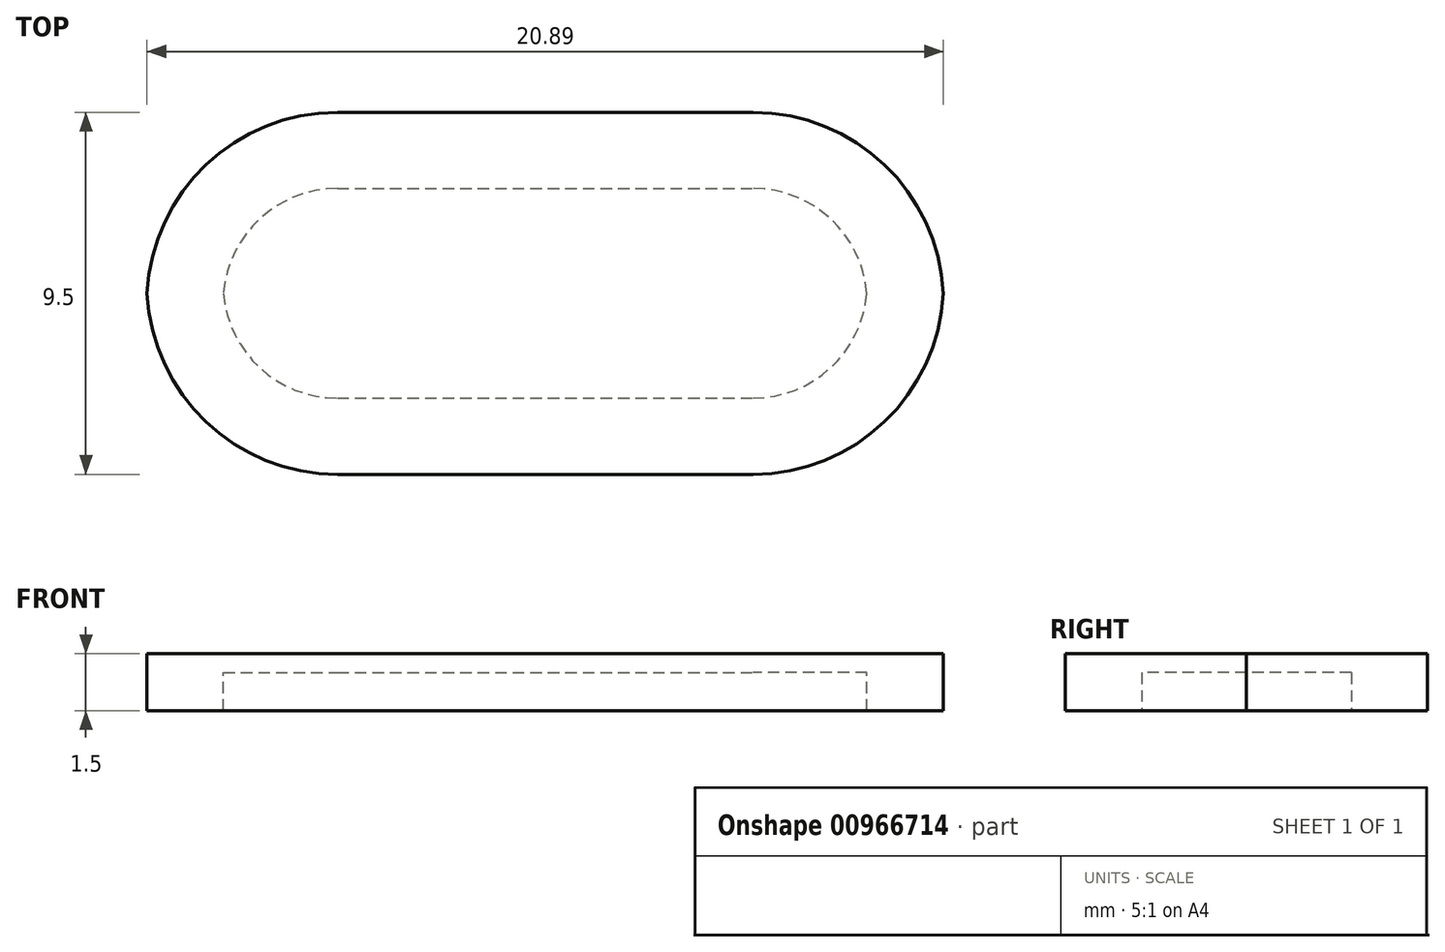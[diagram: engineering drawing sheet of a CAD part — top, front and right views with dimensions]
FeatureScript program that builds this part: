
annotation { "Feature Type Name" : "Feature", "Feature Type Description" : "" }
export const myFeature = defineFeature(function(context is Context, id is Id, definition is map)
    precondition{}
    {
        {
            var Q0;
            Q0=qCreatedBy(makeId("Top.planeOp"),FACE);
            var sketch = newSketch(context, id + "F0", { "sketchPlane" : qUnion([Q0])});
            skLineSegment(sketch, "E0.bottom", {"start": v(-10.3, 4.13) * mm, "end": v(10.6, 4.13) * mm});
            skLineSegment(sketch, "E0.top", {"start": v(-10.3, -5.37) * mm, "end": v(10.6, -5.37) * mm});
            skLineSegment(sketch, "E0.left", {"start": v(-10.3, 4.13) * mm, "end": v(-10.3, -5.37) * mm});
            skLineSegment(sketch, "E0.right", {"start": v(10.6, 4.13) * mm, "end": v(10.6, -5.37) * mm});
            skSolve(sketch);
        }
        {
            var Q0;
            Q0 = qSketchRegion(id + "F0", true);
            extrude(context, id + "F1", {"entities" : qUnion([Q0]), "depth" : 1.5 * mm, "offsetDistance" : 25 * mm});
        }
        {
            var Q0;
            Q0=qCreatedBy(makeId("Top.planeOp"),FACE);
            var sketch = newSketch(context, id + "F2", { "sketchPlane" : qUnion([Q0])});
            skLineSegment(sketch, "E1.bottom", {"start": v(-8.3, 2.13) * mm, "end": v(8.6, 2.13) * mm});
            skLineSegment(sketch, "E1.top", {"start": v(-8.3, -3.37) * mm, "end": v(8.6, -3.37) * mm});
            skLineSegment(sketch, "E1.left", {"start": v(-8.3, 2.13) * mm, "end": v(-8.3, -3.37) * mm});
            skLineSegment(sketch, "E1.right", {"start": v(8.6, 2.13) * mm, "end": v(8.6, -3.37) * mm});
            skSolve(sketch);
        }
        {
            var Q0;
            Q0 = qSketchRegion(id + "F2", true);
            extrude(context, id + "F3", {"entities" : qUnion([Q0]), "operationType" : NewBodyOperationType.REMOVE, "depth" : 1 * mm, "offsetDistance" : 25 * mm});
        }
        {
            var Q0;
            Q0=makeQuery(id+"F3.boolean.opBoolean","COPY",EDGE,{"derivedFrom":makeQuery(id+"F3.opExtrude","SWEPT_EDGE",EDGE,{"disambiguationData":[OSD([sQuery(id+"F2.wireOp",EDGE,"E1.top"),sQuery(id+"F2.wireOp",EDGE,"E1.right")])]})});
            var Q1;
            Q1=makeQuery(id+"F3.boolean.opBoolean","COPY",EDGE,{"derivedFrom":makeQuery(id+"F3.opExtrude","SWEPT_EDGE",EDGE,{"disambiguationData":[OSD([sQuery(id+"F2.wireOp",EDGE,"E1.bottom"),sQuery(id+"F2.wireOp",EDGE,"E1.left")])]})});
            var Q2;
            Q2=makeQuery(id+"F3.boolean.opBoolean","COPY",EDGE,{"derivedFrom":makeQuery(id+"F3.opExtrude","SWEPT_EDGE",EDGE,{"disambiguationData":[OSD([sQuery(id+"F2.wireOp",EDGE,"E1.bottom"),sQuery(id+"F2.wireOp",EDGE,"E1.right")])]})});
            var Q3;
            Q3=makeQuery(id+"F3.boolean.opBoolean","COPY",EDGE,{"derivedFrom":makeQuery(id+"F3.opExtrude","SWEPT_EDGE",EDGE,{"disambiguationData":[OSD([sQuery(id+"F2.wireOp",EDGE,"E1.top"),sQuery(id+"F2.wireOp",EDGE,"E1.left")])]})});
            fillet(context, id + "F4", {"entities" : qUnion([Q0, Q1, Q2, Q3]), "radius" : 3 * mm, "tangentPropagation" : true, "allowEdgeOverflow" : false});
        }
        {
            var Q0;
            Q0=makeQuery(id+"F1.opExtrude","SWEPT_EDGE",EDGE,{"disambiguationData":[OSD([sQuery(id+"F0.wireOp",EDGE,"E0.bottom"),sQuery(id+"F0.wireOp",EDGE,"E0.left")])]});
            var Q1;
            Q1=makeQuery(id+"F1.opExtrude","SWEPT_EDGE",EDGE,{"disambiguationData":[OSD([sQuery(id+"F0.wireOp",EDGE,"E0.top"),sQuery(id+"F0.wireOp",EDGE,"E0.left")])]});
            var Q2;
            Q2=makeQuery(id+"F1.opExtrude","SWEPT_EDGE",EDGE,{"disambiguationData":[OSD([sQuery(id+"F0.wireOp",EDGE,"E0.bottom"),sQuery(id+"F0.wireOp",EDGE,"E0.right")])]});
            var Q3;
            Q3=makeQuery(id+"F1.opExtrude","SWEPT_EDGE",EDGE,{"disambiguationData":[OSD([sQuery(id+"F0.wireOp",EDGE,"E0.top"),sQuery(id+"F0.wireOp",EDGE,"E0.right")])]});
            fillet(context, id + "F5", {"entities" : qUnion([Q0, Q1, Q2, Q3]), "radius" : 5 * mm, "tangentPropagation" : true, "allowEdgeOverflow" : false});
        }
    });
